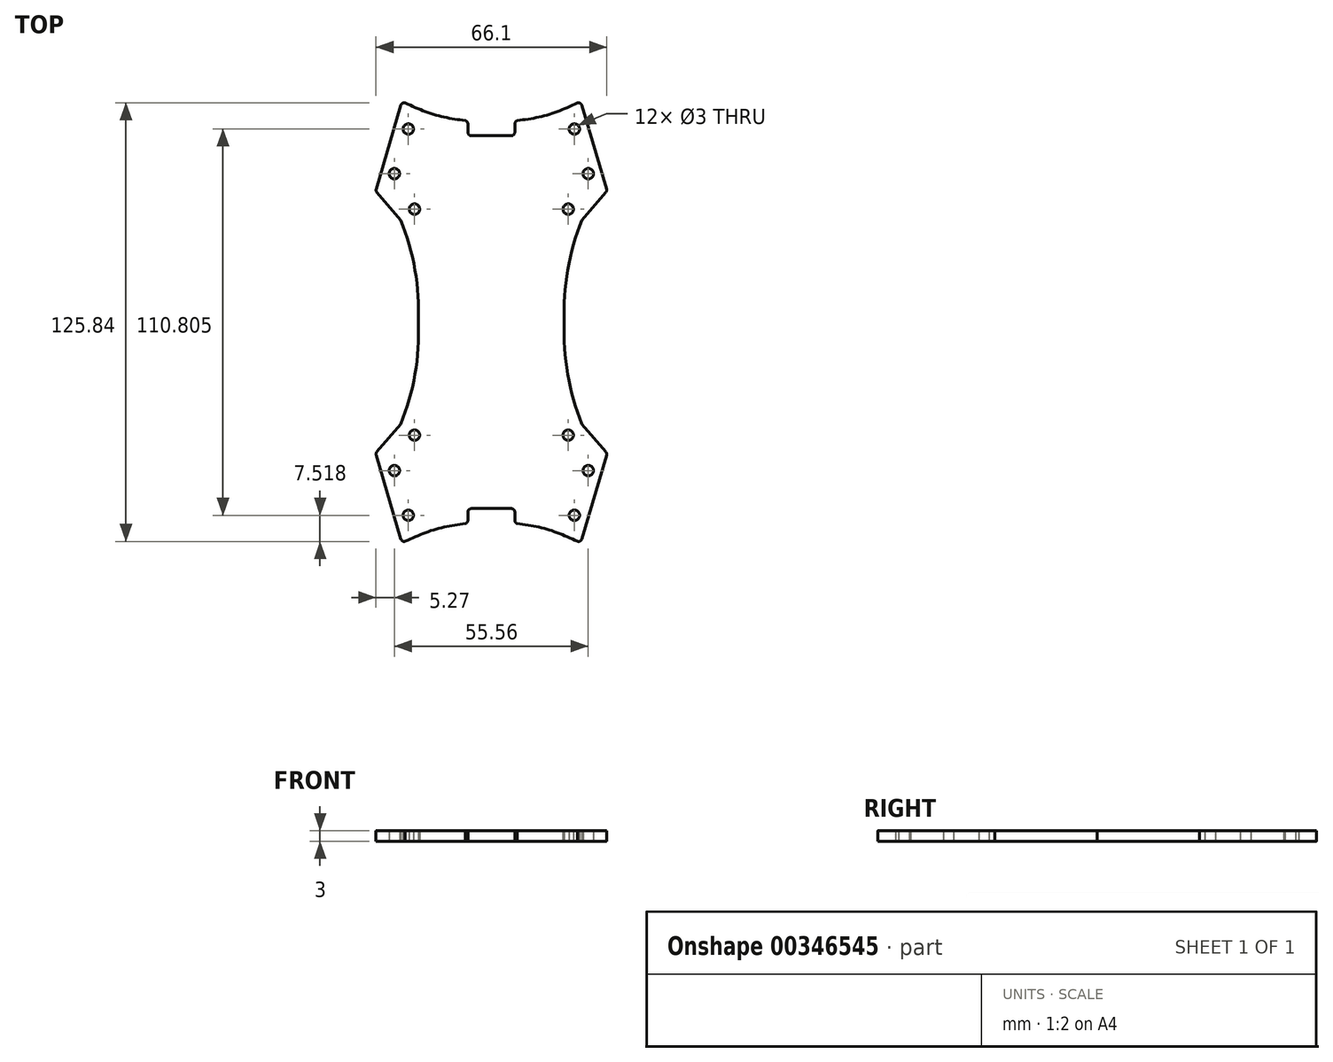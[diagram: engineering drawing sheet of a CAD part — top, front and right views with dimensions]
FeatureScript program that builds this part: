
annotation { "Feature Type Name" : "Feature", "Feature Type Description" : "" }
export const myFeature = defineFeature(function(context is Context, id is Id, definition is map)
    precondition{}
    {
        {
            var Q0;
            Q0=qCreatedBy(makeId("Top.planeOp"),FACE);
            var sketch = newSketch(context, id + "F0", { "sketchPlane" : qUnion([Q0])});
            skPoint(sketch, "E0.middle", {"position": v(0, 0) * mm});
            skCircle(sketch, "E1", {"center": v(-23.8, 55.4) * mm, "radius": 1.5 * mm});
            skCircle(sketch, "E2", {"center": v(-27.78, 42.58) * mm, "radius": 1.5 * mm});
            skCircle(sketch, "E3", {"center": v(-22.03, 32.42) * mm, "radius": 1.5 * mm});
            skLineSegment(sketch, "E4", {"start": v(0, 53.48) * mm, "end": v(-5.73, 53.48) * mm});
            skPoint(sketch, "E4.startSnap0", {"position": v(0, 61) * mm});
            skLineSegment(sketch, "E5", {"start": v(-6.73, 54.48) * mm, "end": v(-6.73, 56.85) * mm});
            skLineSegment(sketch, "E6", {"start": v(-25.93, 62.2) * mm, "end": v(-33, 38.14) * mm});
            skLineSegment(sketch, "E7", {"start": v(-32.8, 37.2) * mm, "end": v(-26, 29.3) * mm});
            skArc(sketch, "E8", {"start": v(-20.93, 0) * mm, "mid": v(-21.87, 14.93) * mm, "end": v(-26, 29.3) * mm});
            skPoint(sketch, "E9.visualSharp", {"position": v(-6.73, 53.48) * mm});
            skArc(sketch, "E9.filletArc", {"start": v(-6.73, 54.48) * mm, "mid": v(-6.43, 53.77) * mm, "end": v(-5.73, 53.48) * mm});
            skPoint(sketch, "E10.visualSharp", {"position": v(-6.73, 57.6) * mm});
            skArc(sketch, "E10.filletArc", {"start": v(-6.73, 56.85) * mm, "mid": v(-6.93, 57.45) * mm, "end": v(-7.45, 57.8) * mm});
            skPoint(sketch, "E11.visualSharp", {"position": v(-25.65, 63.16) * mm});
            skArc(sketch, "E11.filletArc", {"start": v(-24.69, 62.88) * mm, "mid": v(-25.45, 62.8) * mm, "end": v(-25.93, 62.2) * mm});
            skPoint(sketch, "E12.visualSharp", {"position": v(-33.16, 37.62) * mm});
            skArc(sketch, "E12.filletArc", {"start": v(-33, 38.14) * mm, "mid": v(-33.02, 37.65) * mm, "end": v(-32.8, 37.2) * mm});
            skFitSpline(sketch, "E13", {"points": [v(-24.69, 62.88) * mm, v(-16.17, 59.46) * mm, v(-7.45, 57.8) * mm], "startDerivative": vector(16.72, -7.64) * mm, "endDerivative": vector(17.77, -2.49) * mm});
            skLineSegment(sketch, "E14.MirrorCS", {"start": v(0, 53.48) * mm, "end": v(5.73, 53.48) * mm});
            skArc(sketch, "E15.MirrorCS", {"start": v(6.73, 54.48) * mm, "mid": v(6.43, 53.77) * mm, "end": v(5.73, 53.48) * mm});
            skPoint(sketch, "E16.MirrorP", {"position": v(6.73, 53.48) * mm});
            skLineSegment(sketch, "E17.MirrorCS", {"start": v(6.73, 54.48) * mm, "end": v(6.73, 56.85) * mm});
            skArc(sketch, "E18.MirrorCS", {"start": v(6.73, 56.85) * mm, "mid": v(6.93, 57.45) * mm, "end": v(7.45, 57.8) * mm});
            skPoint(sketch, "E19.MirrorP", {"position": v(6.73, 57.6) * mm});
            skFitSpline(sketch, "E20.MirrorCS", {"points": [v(24.69, 62.88) * mm, v(16.17, 59.46) * mm, v(7.45, 57.8) * mm], "startDerivative": vector(-16.72, -7.64) * mm, "endDerivative": vector(-17.77, -2.49) * mm});
            skLineSegment(sketch, "E21.MirrorCS", {"start": v(25.93, 62.2) * mm, "end": v(33, 38.14) * mm});
            skCircle(sketch, "E22.MirrorC", {"center": v(23.8, 55.4) * mm, "radius": 1.5 * mm});
            skArc(sketch, "E23.MirrorCS", {"start": v(24.69, 62.88) * mm, "mid": v(25.45, 62.8) * mm, "end": v(25.93, 62.2) * mm});
            skPoint(sketch, "E24.MirrorP", {"position": v(25.65, 63.16) * mm});
            skCircle(sketch, "E25.MirrorC", {"center": v(27.78, 42.58) * mm, "radius": 1.5 * mm});
            skCircle(sketch, "E26.MirrorC", {"center": v(22.03, 32.42) * mm, "radius": 1.5 * mm});
            skPoint(sketch, "E27.MirrorP", {"position": v(33.16, 37.62) * mm});
            skArc(sketch, "E28.MirrorCS", {"start": v(33, 38.14) * mm, "mid": v(33.02, 37.65) * mm, "end": v(32.8, 37.2) * mm});
            skLineSegment(sketch, "E29.MirrorCS", {"start": v(32.8, 37.2) * mm, "end": v(26, 29.3) * mm});
            skArc(sketch, "E30.MirrorCS", {"start": v(20.93, 0) * mm, "mid": v(21.87, 14.93) * mm, "end": v(26, 29.3) * mm});
            skArc(sketch, "E31.MirrorCS", {"start": v(20.93, 0) * mm, "mid": v(21.87, -14.93) * mm, "end": v(26, -29.3) * mm});
            skArc(sketch, "E32.MirrorCS", {"start": v(-20.93, 0) * mm, "mid": v(-21.87, -14.93) * mm, "end": v(-26, -29.3) * mm});
            skArc(sketch, "E33.MirrorCS", {"start": v(6.73, -56.85) * mm, "mid": v(6.93, -57.45) * mm, "end": v(7.45, -57.8) * mm});
            skArc(sketch, "E34.MirrorCS", {"start": v(6.73, -54.48) * mm, "mid": v(6.43, -53.77) * mm, "end": v(5.73, -53.48) * mm});
            skLineSegment(sketch, "E35.MirrorCS", {"start": v(-6.73, -54.48) * mm, "end": v(-6.73, -56.85) * mm});
            skArc(sketch, "E36.MirrorCS", {"start": v(-6.73, -54.48) * mm, "mid": v(-6.43, -53.77) * mm, "end": v(-5.73, -53.48) * mm});
            skArc(sketch, "E37.MirrorCS", {"start": v(-6.73, -56.85) * mm, "mid": v(-6.93, -57.45) * mm, "end": v(-7.45, -57.8) * mm});
            skLineSegment(sketch, "E38.MirrorCS", {"start": v(6.73, -54.48) * mm, "end": v(6.73, -56.85) * mm});
            skLineSegment(sketch, "E39.MirrorCS", {"start": v(0, -53.48) * mm, "end": v(5.73, -53.48) * mm});
            skLineSegment(sketch, "E40.MirrorCS", {"start": v(25.93, -62.2) * mm, "end": v(33, -38.14) * mm});
            skFitSpline(sketch, "E41.MirrorCS", {"points": [v(24.69, -62.88) * mm, v(16.17, -59.46) * mm, v(7.45, -57.8) * mm], "startDerivative": vector(-16.72, 7.64) * mm, "endDerivative": vector(-17.77, 2.49) * mm});
            skPoint(sketch, "E42.MirrorP", {"position": v(6.73, -57.6) * mm});
            skLineSegment(sketch, "E43.MirrorCS", {"start": v(0, -53.48) * mm, "end": v(-5.73, -53.48) * mm});
            skCircle(sketch, "E44.MirrorC", {"center": v(-23.8, -55.4) * mm, "radius": 1.5 * mm});
            skFitSpline(sketch, "E45.MirrorCS", {"points": [v(-24.69, -62.88) * mm, v(-16.17, -59.46) * mm, v(-7.45, -57.8) * mm], "startDerivative": vector(16.72, 7.64) * mm, "endDerivative": vector(17.77, 2.49) * mm});
            skLineSegment(sketch, "E46.MirrorCS", {"start": v(-25.93, -62.2) * mm, "end": v(-33, -38.14) * mm});
            skPoint(sketch, "E47.MirrorP", {"position": v(-6.73, -53.48) * mm});
            skPoint(sketch, "E48.MirrorP", {"position": v(0, -61) * mm});
            skPoint(sketch, "E49.MirrorP", {"position": v(6.73, -53.48) * mm});
            skCircle(sketch, "E50.MirrorC", {"center": v(23.8, -55.4) * mm, "radius": 1.5 * mm});
            skPoint(sketch, "E51.MirrorP", {"position": v(-6.73, -57.6) * mm});
            skArc(sketch, "E52.MirrorCS", {"start": v(-24.69, -62.88) * mm, "mid": v(-25.45, -62.8) * mm, "end": v(-25.93, -62.2) * mm});
            skPoint(sketch, "E53.MirrorP", {"position": v(-25.65, -63.16) * mm});
            skArc(sketch, "E54.MirrorCS", {"start": v(24.69, -62.88) * mm, "mid": v(25.45, -62.8) * mm, "end": v(25.93, -62.2) * mm});
            skPoint(sketch, "E55.MirrorP", {"position": v(25.65, -63.16) * mm});
            skLineSegment(sketch, "E56.MirrorCS", {"start": v(32.8, -37.2) * mm, "end": v(26, -29.3) * mm});
            skLineSegment(sketch, "E57.MirrorCS", {"start": v(-32.8, -37.2) * mm, "end": v(-26, -29.3) * mm});
            skCircle(sketch, "E58.MirrorC", {"center": v(-27.78, -42.58) * mm, "radius": 1.5 * mm});
            skCircle(sketch, "E59.MirrorC", {"center": v(-22.03, -32.42) * mm, "radius": 1.5 * mm});
            skCircle(sketch, "E60.MirrorC", {"center": v(27.78, -42.58) * mm, "radius": 1.5 * mm});
            skCircle(sketch, "E61.MirrorC", {"center": v(22.03, -32.42) * mm, "radius": 1.5 * mm});
            skPoint(sketch, "E62.trimOffspring.end.orphan", {"position": v(-32.75, 61) * mm});
            skPoint(sketch, "E63.orphan", {"position": v(32.75, 61) * mm});
            skPoint(sketch, "E64.orphan", {"position": v(-32.75, -61) * mm});
            skPoint(sketch, "E0.bottom.start.orphan", {"position": v(32.75, -61) * mm});
            skArc(sketch, "E65.MirrorCS", {"start": v(-33, -38.14) * mm, "mid": v(-33.02, -37.65) * mm, "end": v(-32.8, -37.2) * mm});
            skArc(sketch, "E66.MirrorCS", {"start": v(33, -38.14) * mm, "mid": v(33.02, -37.65) * mm, "end": v(32.8, -37.2) * mm});
            skSolve(sketch);
        }
        {
            var Q0;
            Q0=makeQuery(id+"F0.imprint","IMPRINT",FACE,{"disambiguationData":[TD([[makeQuery(id+"F0.imprint","IMPRINT",EDGE,{"derivedFrom":sQuery(id+"F0.wireOp",EDGE,"E1")}),-1.0]])]});
            extrude(context, id + "F1", {"entities" : qUnion([Q0]), "depth" : 3 * mm});
        }
    });
